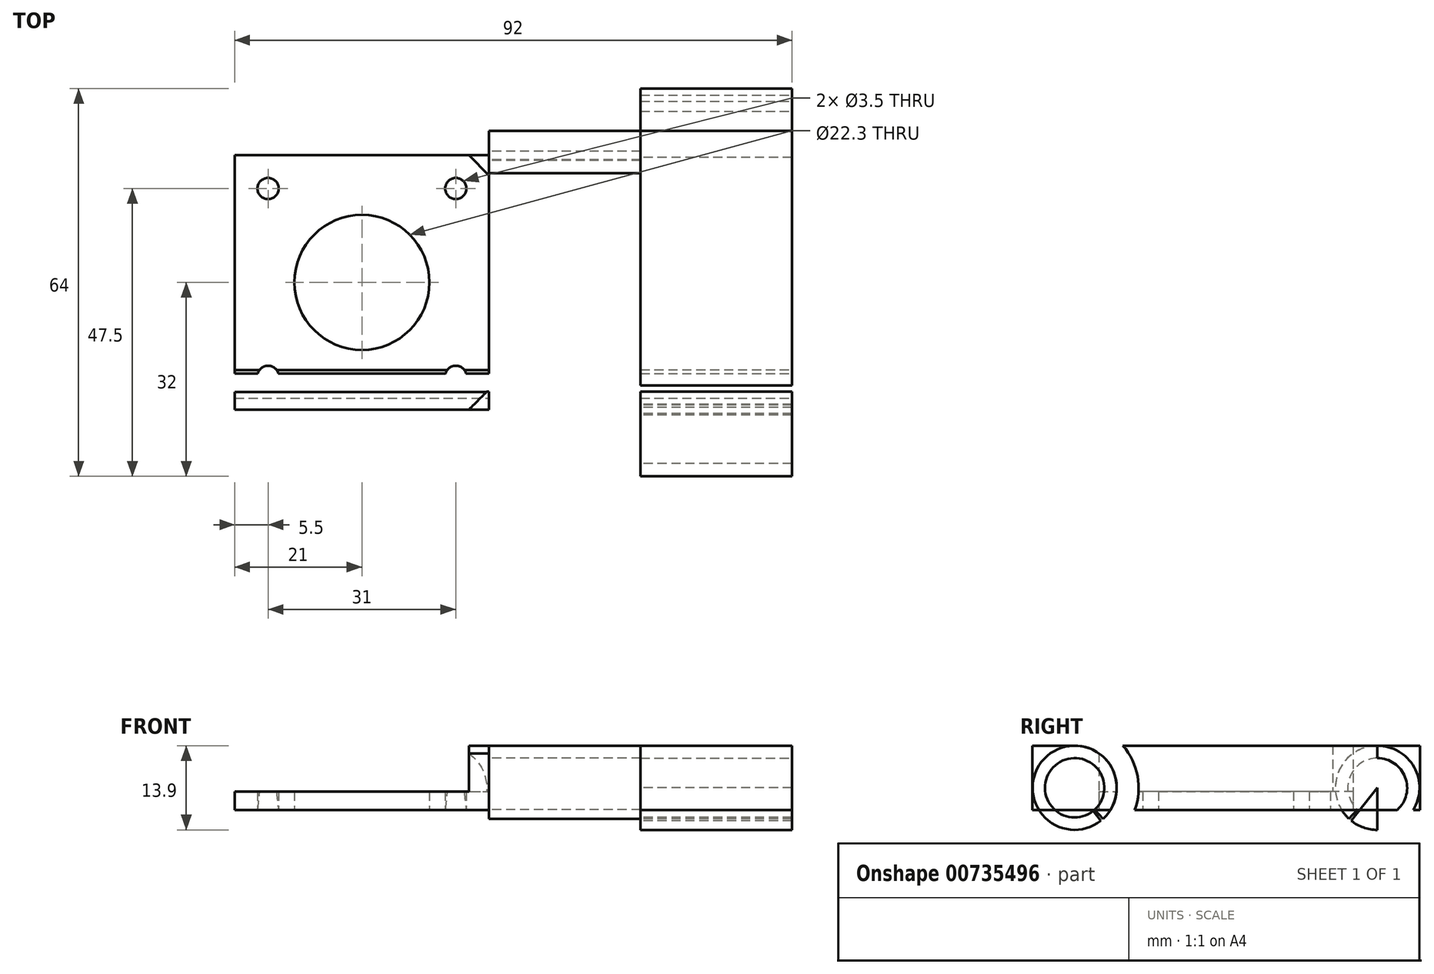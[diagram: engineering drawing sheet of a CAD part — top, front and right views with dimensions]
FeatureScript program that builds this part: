
annotation { "Feature Type Name" : "Feature", "Feature Type Description" : "" }
export const myFeature = defineFeature(function(context is Context, id is Id, definition is map)
    precondition{}
    {
        {
            var Q0;
            Q0=qCreatedBy(makeId("Top.planeOp"),FACE);
            var sketch = newSketch(context, id + "F0", { "sketchPlane" : qUnion([Q0])});
            skLineSegment(sketch, "E0.bottom", {"start": v(-42, 32) * mm, "end": v(50, 32) * mm});
            skLineSegment(sketch, "E0.top", {"start": v(-42, -32) * mm, "end": v(50, -32) * mm});
            skLineSegment(sketch, "E0.left", {"start": v(-42, 32) * mm, "end": v(-42, -32) * mm});
            skLineSegment(sketch, "E0.right", {"start": v(50, 32) * mm, "end": v(50, -32) * mm});
            skCircle(sketch, "E1", {"center": v(-36.5, 15.5) * mm, "radius": 1.75 * mm});
            skCircle(sketch, "E2", {"center": v(-5.5, 15.5) * mm, "radius": 1.75 * mm});
            skCircle(sketch, "E3", {"center": v(-36.5, -15.5) * mm, "radius": 1.75 * mm});
            skCircle(sketch, "E4", {"center": v(-5.5, -15.5) * mm, "radius": 1.75 * mm});
            skLineSegment(sketch, "E5.bottom", {"start": v(50, 32) * mm, "end": v(25, 32) * mm});
            skLineSegment(sketch, "E5.top", {"start": v(50, -32) * mm, "end": v(25, -32) * mm});
            skLineSegment(sketch, "E5.right", {"start": v(25, 32) * mm, "end": v(25, -32) * mm});
            skLineSegment(sketch, "E6.bottom", {"start": v(-42, 21) * mm, "end": v(0, 21) * mm});
            skLineSegment(sketch, "E6.top", {"start": v(-42, -21) * mm, "end": v(0, -21) * mm});
            skLineSegment(sketch, "E6.left", {"start": v(-42, 21) * mm, "end": v(-42, -21) * mm});
            skLineSegment(sketch, "E6.right", {"start": v(0, 21) * mm, "end": v(0, -21) * mm});
            skLineSegment(sketch, "E7", {"start": v(-3.36, 21) * mm, "end": v(0, 17.64) * mm});
            skCircle(sketch, "E8", {"center": v(-21, 0) * mm, "radius": 11.15 * mm});
            skLineSegment(sketch, "E9.MirrorCS", {"start": v(-3.36, -21) * mm, "end": v(0, -17.64) * mm});
            skSolve(sketch);
        }
        {
            var Q0;
            {var subQ9=sQuery(id+"F0.wireOp",EDGE,"E0.bottom");Q0=makeQuery(id+"F0.imprint","IMPRINT",FACE,{"disambiguationData":[TD([[makeQuery(id+"F0.imprint","IMPRINT",EDGE,{"derivedFrom":subQ9}),-1.0]])]});}
            var Q1;
            {var subQ3=sQuery(id+"F0.wireOp",EDGE,"E7");Q1=makeQuery(id+"F0.imprint","IMPRINT",FACE,{"disambiguationData":[TD([[makeQuery(id+"F0.imprint","IMPRINT",EDGE,{"derivedFrom":subQ3}),1.0]])]});}
            var Q2;
            {var subQ3=sQuery(id+"F0.wireOp",EDGE,"oKiCLvQO-OfKN-zIVj-j12f-r2l82N4XMdiO");Q2=makeQuery(id+"F0.imprint","IMPRINT",FACE,{"disambiguationData":[TD([[makeQuery(id+"F0.imprint","IMPRINT",EDGE,{"derivedFrom":subQ3}),-1.0]])]});}
            var Q3;
            Q3=makeQuery(id+"F0.imprint","IMPRINT",FACE,{"disambiguationData":[TD([[makeQuery(id+"F0.imprint","IMPRINT",EDGE,{"derivedFrom":sQuery(id+"F0.wireOp",EDGE,"E5.bottom")}),1.0]])]});
            var Q4;
            {var subQ3=sQuery(id+"F0.wireOp",EDGE,"E9.MirrorCS");Q4=makeQuery(id+"F0.imprint","IMPRINT",FACE,{"disambiguationData":[TD([[makeQuery(id+"F0.imprint","IMPRINT",EDGE,{"derivedFrom":subQ3}),-1.0]])]});}
            extrude(context, id + "F1", {"entities" : qUnion([Q0, Q1, Q2, Q3, Q4]), "depth" : 10.6 * mm, "offsetDistance" : 25 * mm});
        }
        {
            var Q0;
            Q0=makeQuery(id+"F0.imprint","IMPRINT",FACE,{"disambiguationData":[TD([[makeQuery(id+"F0.imprint","IMPRINT",EDGE,{"derivedFrom":sQuery(id+"F0.wireOp",EDGE,"E1")}),-1.0]])]});
            extrude(context, id + "F2", {"entities" : qUnion([Q0]), "operationType" : NewBodyOperationType.ADD, "depth" : 3 * mm, "offsetDistance" : 25 * mm});
        }
        {
            var Q0;
            Q0=qCreatedBy(makeId("Right.planeOp"),FACE);
            var sketch = newSketch(context, id + "F3", { "sketchPlane" : qUnion([Q0])});
            skCircle(sketch, "E10", {"center": v(-25, 3.65) * mm, "radius": 4.9 * mm});
            skLineSegment(sketch, "E11", {"start": v(-25, 3.65) * mm, "end": v(-19.8, -2.84) * mm});
            skLineSegment(sketch, "E12", {"start": v(-25, 3.65) * mm, "end": v(-19.41, -2.4) * mm});
            skLineSegment(sketch, "E13.MirrorCS", {"start": v(25, 3.65) * mm, "end": v(19.41, -2.4) * mm});
            skLineSegment(sketch, "E14.MirrorCS", {"start": v(25, 3.65) * mm, "end": v(19.8, -2.84) * mm});
            skCircle(sketch, "E15.MirrorC", {"center": v(25, 3.65) * mm, "radius": 4.9 * mm});
            skCircle(sketch, "E16", {"center": v(-25, 3.65) * mm, "radius": 6.95 * mm});
            skCircle(sketch, "E17.MirrorC", {"center": v(25, 3.65) * mm, "radius": 6.95 * mm});
            skCircle(sketch, "E18", {"center": v(-25, 3.65) * mm, "radius": 10.57 * mm});
            skCircle(sketch, "E19", {"center": v(25, 3.65) * mm, "radius": 10.64 * mm});
            skLineSegment(sketch, "E20", {"start": v(-25, -6.92) * mm, "end": v(-25, 14.22) * mm});
            skLineSegment(sketch, "E21", {"start": v(25, -6.99) * mm, "end": v(25, 14.29) * mm});
            skSolve(sketch);
        }
        {
            var Q0;
            {var subQ0=sQuery(id+"F3.wireOp",EDGE,"E11");var subQ1=sQuery(id+"F3.wireOp",EDGE,"E10");var subQ2=makeQuery(id+"F3.imprint","INTERSECT",VERTEX,{"derivedFrom":[subQ1,subQ0]});Q0=makeQuery(id+"F3.imprint","IMPRINT",FACE,{"disambiguationData":[TD([[makeQuery(id+"F3.imprint","IMPRINT",EDGE,{"disambiguationData":[TD([[subQ2,1.0]])],"derivedFrom":subQ1}),-1.0]])]});}
            var Q1;
            {var subQ0=sQuery(id+"F3.wireOp",EDGE,"E17.MirrorC");var subQ1=sQuery(id+"F3.wireOp",EDGE,"E13.MirrorCS");var subQ2=makeQuery(id+"F3.imprint","INTERSECT",VERTEX,{"derivedFrom":[subQ1,subQ0]});Q1=makeQuery(id+"F3.imprint","IMPRINT",FACE,{"disambiguationData":[TD([[makeQuery(id+"F3.imprint","IMPRINT",EDGE,{"disambiguationData":[TD([[subQ2,1.0]])],"derivedFrom":subQ1}),-1.0]])]});}
            var Q2;
            {var subQ0=sQuery(id+"F3.wireOp",EDGE,"E17.MirrorC");var subQ1=sQuery(id+"F3.wireOp",EDGE,"E14.MirrorCS");var subQ2=makeQuery(id+"F3.imprint","INTERSECT",VERTEX,{"derivedFrom":[subQ1,subQ0]});Q2=makeQuery(id+"F3.imprint","IMPRINT",FACE,{"disambiguationData":[TD([[makeQuery(id+"F3.imprint","IMPRINT",EDGE,{"disambiguationData":[TD([[subQ2,1.0]])],"derivedFrom":subQ1}),1.0]])]});}
            var Q3;
            {var subQ0=sQuery(id+"F3.wireOp",EDGE,"E21");var subQ1=sQuery(id+"F3.wireOp",EDGE,"E15.MirrorC");var subQ2=makeQuery(id+"F3.imprint","INTERSECT",VERTEX,{"disambiguationData":[OD(0.0)],"derivedFrom":[subQ1,subQ0]});Q3=makeQuery(id+"F3.imprint","IMPRINT",FACE,{"disambiguationData":[TD([[makeQuery(id+"F3.imprint","IMPRINT",EDGE,{"disambiguationData":[TD([[subQ2,1.0]])],"derivedFrom":subQ1}),1.0]])]});}
            var Q4;
            {var subQ0=sQuery(id+"F3.wireOp",EDGE,"E20");var subQ1=sQuery(id+"F3.wireOp",EDGE,"E10");var subQ2=makeQuery(id+"F3.imprint","INTERSECT",VERTEX,{"disambiguationData":[OD(0.0)],"derivedFrom":[subQ1,subQ0]});Q4=makeQuery(id+"F3.imprint","IMPRINT",FACE,{"disambiguationData":[TD([[makeQuery(id+"F3.imprint","IMPRINT",EDGE,{"disambiguationData":[TD([[subQ2,1.0]])],"derivedFrom":subQ1}),-1.0]])]});}
            var Q5;
            {var subQ0=sQuery(id+"F3.wireOp",EDGE,"E20");var subQ1=sQuery(id+"F3.wireOp",EDGE,"E10");var subQ2=makeQuery(id+"F3.imprint","INTERSECT",VERTEX,{"disambiguationData":[OD(1.0)],"derivedFrom":[subQ1,subQ0]});Q5=makeQuery(id+"F3.imprint","IMPRINT",FACE,{"disambiguationData":[TD([[makeQuery(id+"F3.imprint","IMPRINT",EDGE,{"disambiguationData":[TD([[subQ2,1.0]])],"derivedFrom":subQ1}),-1.0]])]});}
            var Q6;
            Q6=sQuery(id+"F3.wireOp",EDGE,"71ff0334-b54f-48c9-bb58-b5a2ff3522fb");
            var Q7;
            Q7=sQuery(id+"F3.wireOp",EDGE,"E10");
            extrude(context, id + "F4", {"entities" : qUnion([Q0, Q1, Q2, Q3, Q4, Q5]), "surfaceEntities" : qUnion([Q6, Q7]), "depth" : 25 * mm, "offsetDistance" : 25 * mm});
        }
        {
            var Q0;
            Q0=makeQuery(id+"F4.opExtrude","SWEPT_BODY",BODY,{"disambiguationData":[OSD([sQuery(id+"F3.wireOp",EDGE,"E10"),sQuery(id+"F3.wireOp",EDGE,"Tpk7JWVg-47xD-8qUS-Kruc-J8CiNJftMKC9.bottom"),sQuery(id+"F3.wireOp",EDGE,"Tpk7JWVg-47xD-8qUS-Kruc-J8CiNJftMKC9.top"),sQuery(id+"F3.wireOp",EDGE,"Tpk7JWVg-47xD-8qUS-Kruc-J8CiNJftMKC9.left"),sQuery(id+"F3.wireOp",EDGE,"Tpk7JWVg-47xD-8qUS-Kruc-J8CiNJftMKC9.right"),sQuery(id+"F3.wireOp",EDGE,"E11")])]});
            var Q1;
            Q1=makeQuery(id+"F4.opExtrude","SWEPT_BODY",BODY,{"disambiguationData":[OSD([sQuery(id+"F3.wireOp",EDGE,"2d4acbe7-4071-4dab-a98e-cb93f226dd8a0.MirrorCS"),sQuery(id+"F3.wireOp",EDGE,"2d4acbe7-4071-4dab-a98e-cb93f226dd8a1.MirrorCS"),sQuery(id+"F3.wireOp",EDGE,"2d4acbe7-4071-4dab-a98e-cb93f226dd8a2.MirrorCS"),sQuery(id+"F3.wireOp",EDGE,"2d4acbe7-4071-4dab-a98e-cb93f226dd8a3.MirrorCS"),sQuery(id+"F3.wireOp",EDGE,"E14.MirrorCS"),sQuery(id+"F3.wireOp",EDGE,"E15.MirrorC")])]});
            transform(context, id + "F5", {"entities" : qUnion([Q0, Q1]), "transformType" : TransformType.TRANSLATION_3D, "dx" : 25 * mm, "dy" : 0 * mm, "dz" : 0 * mm, "makeCopy" : false});
        }
        {
            var Q0;
            {var subQ0=sQuery(id+"F3.wireOp",EDGE,"E20");var subQ1=sQuery(id+"F3.wireOp",EDGE,"E10");var subQ2=makeQuery(id+"F3.imprint","INTERSECT",VERTEX,{"disambiguationData":[OD(0.0)],"derivedFrom":[subQ1,subQ0]});Q0=makeQuery(id+"F3.imprint","IMPRINT",FACE,{"disambiguationData":[TD([[makeQuery(id+"F3.imprint","IMPRINT",EDGE,{"disambiguationData":[TD([[subQ2,1.0]])],"derivedFrom":subQ1}),1.0]])]});}
            var Q1;
            {var subQ0=sQuery(id+"F3.wireOp",EDGE,"E21");var subQ1=sQuery(id+"F3.wireOp",EDGE,"E15.MirrorC");var subQ2=makeQuery(id+"F3.imprint","INTERSECT",VERTEX,{"disambiguationData":[OD(0.0)],"derivedFrom":[subQ1,subQ0]});Q1=makeQuery(id+"F3.imprint","IMPRINT",FACE,{"disambiguationData":[TD([[makeQuery(id+"F3.imprint","IMPRINT",EDGE,{"disambiguationData":[TD([[subQ2,1.0]])],"derivedFrom":subQ1}),-1.0]])]});}
            var Q2;
            {var subQ1=sQuery(id+"F3.wireOp",EDGE,"E13.MirrorCS");var subQ3=sQuery(id+"F3.wireOp",EDGE,"E15.MirrorC");var subQ4=makeQuery(id+"F3.imprint","INTERSECT",VERTEX,{"derivedFrom":[subQ1,subQ3]});Q2=makeQuery(id+"F3.imprint","IMPRINT",FACE,{"disambiguationData":[TD([[makeQuery(id+"F3.imprint","IMPRINT",EDGE,{"disambiguationData":[TD([[subQ4,-1.0]])],"derivedFrom":subQ3}),-1.0]])]});}
            var Q3;
            {var subQ1=sQuery(id+"F3.wireOp",EDGE,"E13.MirrorCS");var subQ3=sQuery(id+"F3.wireOp",EDGE,"E15.MirrorC");var subQ4=makeQuery(id+"F3.imprint","INTERSECT",VERTEX,{"derivedFrom":[subQ1,subQ3]});Q3=makeQuery(id+"F3.imprint","IMPRINT",FACE,{"disambiguationData":[TD([[makeQuery(id+"F3.imprint","IMPRINT",EDGE,{"disambiguationData":[TD([[subQ4,1.0]])],"derivedFrom":subQ3}),-1.0]])]});}
            var Q4;
            {var subQ1=sQuery(id+"F3.wireOp",EDGE,"E14.MirrorCS");var subQ3=sQuery(id+"F3.wireOp",EDGE,"E15.MirrorC");var subQ4=makeQuery(id+"F3.imprint","INTERSECT",VERTEX,{"derivedFrom":[subQ1,subQ3]});Q4=makeQuery(id+"F3.imprint","IMPRINT",FACE,{"disambiguationData":[TD([[makeQuery(id+"F3.imprint","IMPRINT",EDGE,{"disambiguationData":[TD([[subQ4,1.0]])],"derivedFrom":subQ3}),-1.0]])]});}
            var Q5;
            {var subQ0=sQuery(id+"F3.wireOp",EDGE,"E20");var subQ1=sQuery(id+"F3.wireOp",EDGE,"E10");var subQ2=makeQuery(id+"F3.imprint","INTERSECT",VERTEX,{"disambiguationData":[OD(1.0)],"derivedFrom":[subQ1,subQ0]});Q5=makeQuery(id+"F3.imprint","IMPRINT",FACE,{"disambiguationData":[TD([[makeQuery(id+"F3.imprint","IMPRINT",EDGE,{"disambiguationData":[TD([[subQ2,1.0]])],"derivedFrom":subQ1}),1.0]])]});}
            var Q6;
            {var subQ0=sQuery(id+"F3.wireOp",EDGE,"E20");var subQ1=sQuery(id+"F3.wireOp",EDGE,"E10");var subQ2=makeQuery(id+"F3.imprint","INTERSECT",VERTEX,{"disambiguationData":[OD(0.0)],"derivedFrom":[subQ1,subQ0]});Q6=makeQuery(id+"F3.imprint","IMPRINT",FACE,{"disambiguationData":[TD([[makeQuery(id+"F3.imprint","IMPRINT",EDGE,{"disambiguationData":[TD([[subQ2,-1.0]])],"derivedFrom":subQ1}),1.0]])]});}
            var Q7;
            {var subQ0=sQuery(id+"F3.wireOp",EDGE,"E11");var subQ1=sQuery(id+"F3.wireOp",EDGE,"E10");var subQ2=makeQuery(id+"F3.imprint","INTERSECT",VERTEX,{"derivedFrom":[subQ1,subQ0]});Q7=makeQuery(id+"F3.imprint","IMPRINT",FACE,{"disambiguationData":[TD([[makeQuery(id+"F3.imprint","IMPRINT",EDGE,{"disambiguationData":[TD([[subQ2,-1.0]])],"derivedFrom":subQ1}),1.0]])]});}
            extrude(context, id + "F6", {"entities" : qUnion([Q0, Q1, Q2, Q3, Q4, Q5, Q6, Q7]), "depth" : 26 * mm, "offsetDistance" : 25 * mm});
        }
        {
            var Q0;
            Q0=makeQuery(id+"F6.opExtrude","SWEPT_BODY",BODY,{"disambiguationData":[OSD([sQuery(id+"F3.wireOp",EDGE,"E10")])]});
            var Q1;
            Q1=makeQuery(id+"F6.opExtrude","SWEPT_BODY",BODY,{"disambiguationData":[OSD([sQuery(id+"F3.wireOp",EDGE,"E15.MirrorC")])]});
            transform(context, id + "F7", {"entities" : qUnion([Q0, Q1]), "transformType" : TransformType.TRANSLATION_3D, "dx" : 24 * mm, "dy" : 0 * mm, "dz" : 0 * mm, "makeCopy" : false});
        }
        {
            var Q0;
            {var subQ0=sQuery(id+"F3.wireOp",EDGE,"E11");var subQ1=sQuery(id+"F3.wireOp",EDGE,"E10");var subQ2=makeQuery(id+"F3.imprint","INTERSECT",VERTEX,{"derivedFrom":[subQ1,subQ0]});Q0=makeQuery(id+"F3.imprint","IMPRINT",FACE,{"disambiguationData":[TD([[makeQuery(id+"F3.imprint","IMPRINT",EDGE,{"disambiguationData":[TD([[subQ2,-1.0]])],"derivedFrom":subQ1}),-1.0]])]});}
            var Q1;
            {var subQ0=sQuery(id+"F3.wireOp",EDGE,"E17.MirrorC");var subQ1=sQuery(id+"F3.wireOp",EDGE,"E13.MirrorCS");var subQ2=makeQuery(id+"F3.imprint","INTERSECT",VERTEX,{"derivedFrom":[subQ1,subQ0]});Q1=makeQuery(id+"F3.imprint","IMPRINT",FACE,{"disambiguationData":[TD([[makeQuery(id+"F3.imprint","IMPRINT",EDGE,{"disambiguationData":[TD([[subQ2,1.0]])],"derivedFrom":subQ1}),1.0]])]});}
            extrude(context, id + "F8", {"entities" : qUnion([Q0, Q1]), "depth" : 25 * mm, "offsetDistance" : 25 * mm});
        }
        {
            var Q0;
            Q0=makeQuery(id+"F8.opExtrude","SWEPT_BODY",BODY,{"disambiguationData":[OSD([sQuery(id+"F3.wireOp",EDGE,"2d4acbe7-4071-4dab-a98e-cb93f226dd8a0.MirrorCS"),sQuery(id+"F3.wireOp",EDGE,"2d4acbe7-4071-4dab-a98e-cb93f226dd8a3.MirrorCS"),sQuery(id+"F3.wireOp",EDGE,"E13.MirrorCS"),sQuery(id+"F3.wireOp",EDGE,"E14.MirrorCS"),sQuery(id+"F3.wireOp",EDGE,"E15.MirrorC"),sQuery(id+"F3.wireOp",EDGE,"WBvfeIdI-CzTW-o9ny-GBJM-GZW4FtTWXN8o")])]});
            var Q1;
            Q1=makeQuery(id+"F8.opExtrude","SWEPT_BODY",BODY,{"disambiguationData":[OSD([sQuery(id+"F3.wireOp",EDGE,"E10"),sQuery(id+"F3.wireOp",EDGE,"Tpk7JWVg-47xD-8qUS-Kruc-J8CiNJftMKC9.bottom"),sQuery(id+"F3.wireOp",EDGE,"Tpk7JWVg-47xD-8qUS-Kruc-J8CiNJftMKC9.right"),sQuery(id+"F3.wireOp",EDGE,"E11"),sQuery(id+"F3.wireOp",EDGE,"E12"),sQuery(id+"F3.wireOp",EDGE,"Ll1rp7AC-GtAV-Mc3y-4FNo-Jx5HDOu18Eyv")])]});
            transform(context, id + "F9", {"entities" : qUnion([Q0, Q1]), "transformType" : TransformType.TRANSLATION_3D, "dx" : 25 * mm, "dy" : 0 * mm, "dz" : 0 * mm, "makeCopy" : false});
        }
        {
            var Q0;
            Q0=makeQuery(id+"F6.opExtrude","SWEPT_BODY",BODY,{"disambiguationData":[OSD([sQuery(id+"F3.wireOp",EDGE,"E10"),sQuery(id+"F3.wireOp",EDGE,"E11"),sQuery(id+"F3.wireOp",EDGE,"E12")])]});
            var Q1;
            Q1=makeQuery(id+"F6.opExtrude","SWEPT_BODY",BODY,{"disambiguationData":[OSD([sQuery(id+"F3.wireOp",EDGE,"E13.MirrorCS"),sQuery(id+"F3.wireOp",EDGE,"E14.MirrorCS"),sQuery(id+"F3.wireOp",EDGE,"E15.MirrorC")])]});
            var Q2;
            Q2=makeQuery(id+"F8.opExtrude","SWEPT_BODY",BODY,{"disambiguationData":[OSD([sQuery(id+"F3.wireOp",EDGE,"E13.MirrorCS"),sQuery(id+"F3.wireOp",EDGE,"E14.MirrorCS"),sQuery(id+"F3.wireOp",EDGE,"E15.MirrorC"),sQuery(id+"F3.wireOp",EDGE,"E17.MirrorC")])]});
            var Q3;
            Q3=makeQuery(id+"F8.opExtrude","SWEPT_BODY",BODY,{"disambiguationData":[OSD([sQuery(id+"F3.wireOp",EDGE,"E10"),sQuery(id+"F3.wireOp",EDGE,"E11"),sQuery(id+"F3.wireOp",EDGE,"E12"),sQuery(id+"F3.wireOp",EDGE,"E16")])]});
            var Q4;
            Q4=makeQuery(id+"F1.opExtrude","SWEPT_BODY",BODY,{"disambiguationData":[OSD([sQuery(id+"F0.wireOp",EDGE,"E0.bottom"),sQuery(id+"F0.wireOp",EDGE,"E0.top"),sQuery(id+"F0.wireOp",EDGE,"E0.left"),sQuery(id+"F0.wireOp",EDGE,"E5.bottom"),sQuery(id+"F0.wireOp",EDGE,"E5.top"),sQuery(id+"F0.wireOp",EDGE,"E0.right"),sQuery(id+"F0.wireOp",EDGE,"E6.bottom"),sQuery(id+"F0.wireOp",EDGE,"E6.top"),sQuery(id+"F0.wireOp",EDGE,"E6.right"),sQuery(id+"F0.wireOp",EDGE,"E7"),sQuery(id+"F0.wireOp",EDGE,"oKiCLvQO-OfKN-zIVj-j12f-r2l82N4XMdiO")])]});
            booleanBodies(context, id + "F10", {"operationType" : BooleanOperationType.SUBTRACTION, "tools" : qUnion([Q0, Q1, Q2, Q3]), "targets" : qUnion([Q4])});
        }
        {
            var Q0;
            {var subQ0=sQuery(id+"F3.wireOp",EDGE,"E20");var subQ1=sQuery(id+"F3.wireOp",EDGE,"E16");var subQ2=makeQuery(id+"F3.imprint","INTERSECT",VERTEX,{"disambiguationData":[OD(0.0)],"derivedFrom":[subQ1,subQ0]});Q0=makeQuery(id+"F3.imprint","IMPRINT",FACE,{"disambiguationData":[TD([[makeQuery(id+"F3.imprint","IMPRINT",EDGE,{"disambiguationData":[TD([[subQ2,1.0]])],"derivedFrom":subQ1}),-1.0]])]});}
            var Q1;
            {var subQ0=sQuery(id+"F3.wireOp",EDGE,"E21");var subQ1=sQuery(id+"F3.wireOp",EDGE,"E17.MirrorC");var subQ2=makeQuery(id+"F3.imprint","INTERSECT",VERTEX,{"disambiguationData":[OD(0.0)],"derivedFrom":[subQ1,subQ0]});Q1=makeQuery(id+"F3.imprint","IMPRINT",FACE,{"disambiguationData":[TD([[makeQuery(id+"F3.imprint","IMPRINT",EDGE,{"disambiguationData":[TD([[subQ2,1.0]])],"derivedFrom":subQ1}),1.0]])]});}
            extrude(context, id + "F11", {"entities" : qUnion([Q0, Q1]), "operationType" : NewBodyOperationType.REMOVE, "endBound" : BoundingType.SYMMETRIC, "oppositeDirection" : true, "depth" : 100 * mm, "offsetDistance" : 25 * mm});
        }
        {
            var Q0;
            Q0=qCreatedBy(makeId("Top.planeOp"),FACE);
            var sketch = newSketch(context, id + "F12", { "sketchPlane" : qUnion([Q0])});
            skCircle(sketch, "E22", {"center": v(8.8, -11.5) * mm, "radius": 2.5 * mm});
            skCircle(sketch, "E23.MirrorC", {"center": v(8.8, 11.5) * mm, "radius": 2.5 * mm});
            skSolve(sketch);
        }
        {
            var Q0;
            Q0 = qSketchRegion(id + "F12", true);
            extrude(context, id + "F13", {"entities" : qUnion([Q0]), "operationType" : NewBodyOperationType.REMOVE, "depth" : 15 * mm, "offsetDistance" : 25 * mm});
        }
    });
